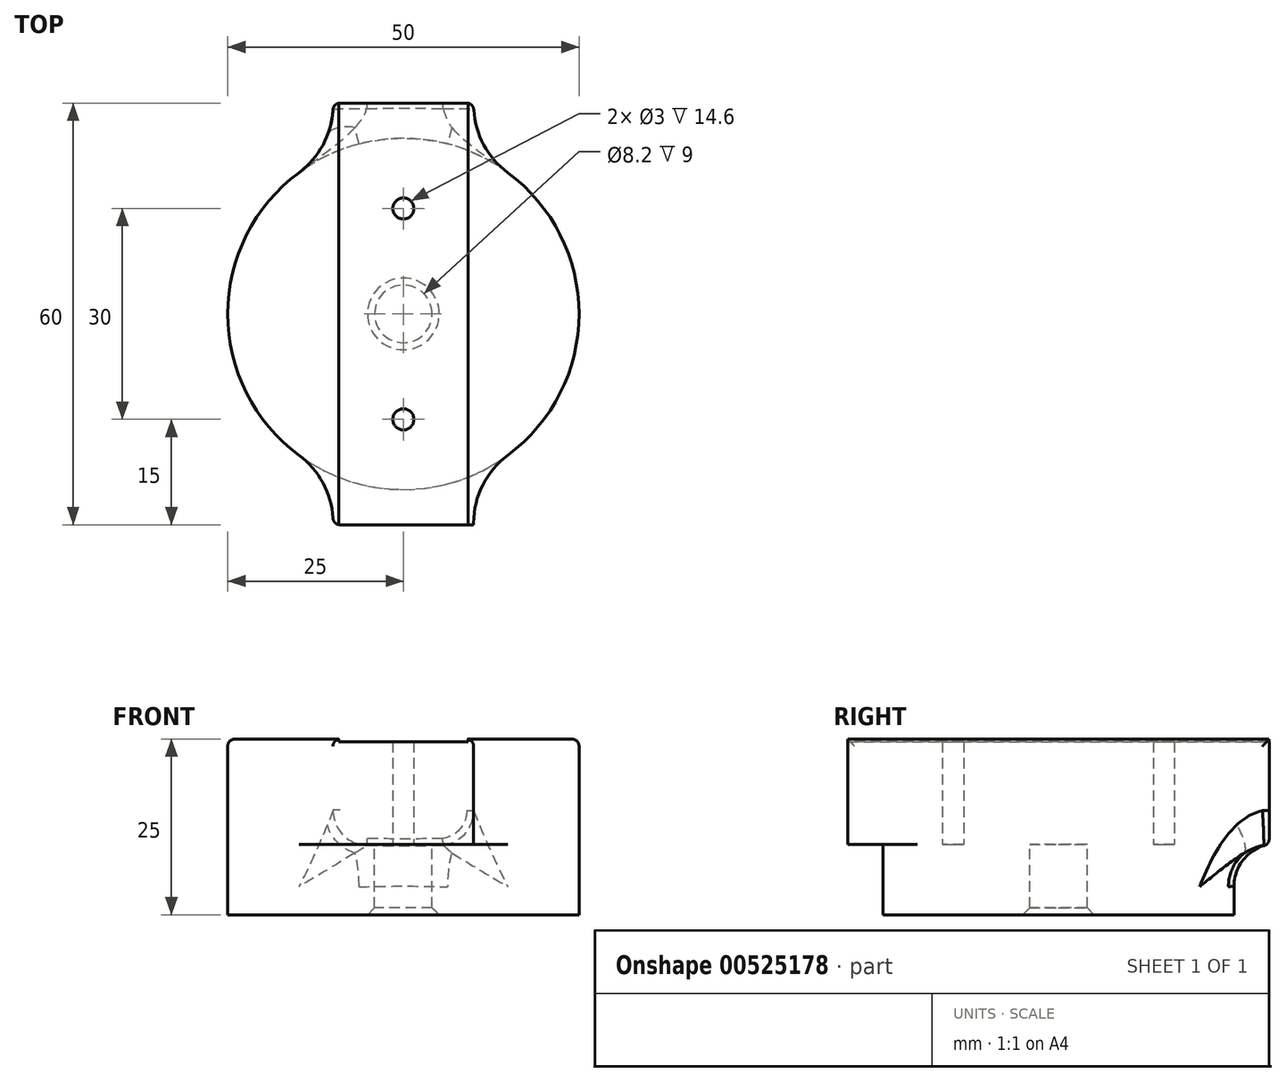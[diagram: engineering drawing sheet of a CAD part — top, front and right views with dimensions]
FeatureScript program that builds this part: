
annotation { "Feature Type Name" : "Feature", "Feature Type Description" : "" }
export const myFeature = defineFeature(function(context is Context, id is Id, definition is map)
    precondition{}
    {
        {
            var Q0;
            Q0=qCreatedBy(makeId("Top.planeOp"),FACE);
            var sketch = newSketch(context, id + "F0", { "sketchPlane" : qUnion([Q0])});
            skLineSegment(sketch, "E0.bottom", {"start": v(-10, 0) * mm, "end": v(10, 0) * mm});
            skLineSegment(sketch, "E0.top", {"start": v(-10, 30) * mm, "end": v(10, 30) * mm});
            skLineSegment(sketch, "E0.left", {"start": v(-10, 0) * mm, "end": v(-10, 30) * mm});
            skLineSegment(sketch, "E0.right", {"start": v(10, 0) * mm, "end": v(10, 30) * mm});
            skCircle(sketch, "E1", {"center": v(0, 15) * mm, "radius": 1.5 * mm});
            skCircle(sketch, "E2", {"center": v(0, 0) * mm, "radius": 25 * mm});
            skCircle(sketch, "E3", {"center": v(0, 0) * mm, "radius": 4.1 * mm});
            skLineSegment(sketch, "E4.1.0", {"start": v(10, -30) * mm, "end": v(-10, -30) * mm});
            skLineSegment(sketch, "E4.1.1", {"start": v(10, 0) * mm, "end": v(10, -30) * mm});
            skLineSegment(sketch, "E4.1.2", {"start": v(-10, 0) * mm, "end": v(-10, -30) * mm});
            skCircle(sketch, "E4.1.3", {"center": v(0, -15) * mm, "radius": 1.5 * mm});
            skSolve(sketch);
        }
        {
            var Q0;
            {var subQ1=sQuery(id+"F0.wireOp",EDGE,"E0.right");var subQ3=sQuery(id+"F0.wireOp",EDGE,"E2");var subQ4=makeQuery(id+"F0.imprint","INTERSECT",VERTEX,{"derivedFrom":[subQ1,subQ3]});Q0=makeQuery(id+"F0.imprint","IMPRINT",FACE,{"disambiguationData":[TD([[makeQuery(id+"F0.imprint","IMPRINT",EDGE,{"disambiguationData":[TD([[subQ4,1.0]])],"derivedFrom":subQ3}),1.0]])]});}
            var Q1;
            {var subQ1=sQuery(id+"F0.wireOp",EDGE,"E0.left");var subQ3=sQuery(id+"F0.wireOp",EDGE,"E2");var subQ4=makeQuery(id+"F0.imprint","INTERSECT",VERTEX,{"derivedFrom":[subQ1,subQ3]});Q1=makeQuery(id+"F0.imprint","IMPRINT",FACE,{"disambiguationData":[TD([[makeQuery(id+"F0.imprint","IMPRINT",EDGE,{"disambiguationData":[TD([[subQ4,-1.0]])],"derivedFrom":subQ3}),1.0]])]});}
            var Q2;
            Q2=makeQuery(id+"F0.imprint","IMPRINT",FACE,{"disambiguationData":[TD([[makeQuery(id+"F0.imprint","IMPRINT",EDGE,{"derivedFrom":sQuery(id+"F0.wireOp",EDGE,"E1")}),-1.0]])]});
            var Q3;
            {var subQ5=sQuery(id+"F0.wireOp",EDGE,"E4.1.0");Q3=makeQuery(id+"F0.imprint","IMPRINT",FACE,{"disambiguationData":[TD([[makeQuery(id+"F0.imprint","IMPRINT",EDGE,{"derivedFrom":subQ5}),-1.0]])]});}
            var Q4;
            Q4=makeQuery(id+"F0.imprint","IMPRINT",FACE,{"disambiguationData":[TD([[makeQuery(id+"F0.imprint","IMPRINT",EDGE,{"derivedFrom":sQuery(id+"F0.wireOp",EDGE,"E4.1.3")}),-1.0]])]});
            var Q5;
            {var subQ0=sQuery(id+"F0.wireOp",EDGE,"E3");var subQ1=sQuery(id+"F0.wireOp",EDGE,"E0.bottom");var subQ2=makeQuery(id+"F0.imprint","INTERSECT",VERTEX,{"disambiguationData":[OD(0.0)],"derivedFrom":[subQ1,subQ0]});Q5=makeQuery(id+"F0.imprint","IMPRINT",FACE,{"disambiguationData":[TD([[makeQuery(id+"F0.imprint","IMPRINT",EDGE,{"disambiguationData":[TD([[subQ2,-1.0]])],"derivedFrom":subQ1}),1.0]])]});}
            var Q6;
            {var subQ0=sQuery(id+"F0.wireOp",EDGE,"E3");var subQ1=sQuery(id+"F0.wireOp",EDGE,"E0.bottom");var subQ2=makeQuery(id+"F0.imprint","INTERSECT",VERTEX,{"disambiguationData":[OD(0.0)],"derivedFrom":[subQ1,subQ0]});Q6=makeQuery(id+"F0.imprint","IMPRINT",FACE,{"disambiguationData":[TD([[makeQuery(id+"F0.imprint","IMPRINT",EDGE,{"disambiguationData":[TD([[subQ2,-1.0]])],"derivedFrom":subQ1}),-1.0]])]});}
            var Q7;
            {var subQ0=sQuery(id+"F0.wireOp",EDGE,"E0.top");Q7=makeQuery(id+"F0.imprint","IMPRINT",FACE,{"disambiguationData":[TD([[makeQuery(id+"F0.imprint","IMPRINT",EDGE,{"derivedFrom":subQ0}),-1.0]])]});}
            extrude(context, id + "F1", {"entities" : qUnion([Q0, Q1, Q2, Q3, Q4, Q5, Q6, Q7]), "depth" : 14.6 * mm, "offsetDistance" : 25 * mm});
        }
        {
            var Q0;
            {var subQ1=sQuery(id+"F0.wireOp",EDGE,"E0.right");var subQ3=sQuery(id+"F0.wireOp",EDGE,"E2");var subQ4=makeQuery(id+"F0.imprint","INTERSECT",VERTEX,{"derivedFrom":[subQ1,subQ3]});Q0=makeQuery(id+"F0.imprint","IMPRINT",FACE,{"disambiguationData":[TD([[makeQuery(id+"F0.imprint","IMPRINT",EDGE,{"disambiguationData":[TD([[subQ4,1.0]])],"derivedFrom":subQ3}),1.0]])]});}
            var Q1;
            Q1=makeQuery(id+"F0.imprint","IMPRINT",FACE,{"disambiguationData":[TD([[makeQuery(id+"F0.imprint","IMPRINT",EDGE,{"derivedFrom":sQuery(id+"F0.wireOp",EDGE,"E4.1.3")}),-1.0]])]});
            var Q2;
            {var subQ1=sQuery(id+"F0.wireOp",EDGE,"E0.left");var subQ3=sQuery(id+"F0.wireOp",EDGE,"E2");var subQ4=makeQuery(id+"F0.imprint","INTERSECT",VERTEX,{"derivedFrom":[subQ1,subQ3]});Q2=makeQuery(id+"F0.imprint","IMPRINT",FACE,{"disambiguationData":[TD([[makeQuery(id+"F0.imprint","IMPRINT",EDGE,{"disambiguationData":[TD([[subQ4,-1.0]])],"derivedFrom":subQ3}),1.0]])]});}
            var Q3;
            Q3=makeQuery(id+"F0.imprint","IMPRINT",FACE,{"disambiguationData":[TD([[makeQuery(id+"F0.imprint","IMPRINT",EDGE,{"derivedFrom":sQuery(id+"F0.wireOp",EDGE,"E4.1.3")}),1.0]])]});
            var Q4;
            Q4=makeQuery(id+"F0.imprint","IMPRINT",FACE,{"disambiguationData":[TD([[makeQuery(id+"F0.imprint","IMPRINT",EDGE,{"derivedFrom":sQuery(id+"F0.wireOp",EDGE,"E1")}),-1.0]])]});
            var Q5;
            Q5=makeQuery(id+"F0.imprint","IMPRINT",FACE,{"disambiguationData":[TD([[makeQuery(id+"F0.imprint","IMPRINT",EDGE,{"derivedFrom":sQuery(id+"F0.wireOp",EDGE,"E1")}),1.0]])]});
            extrude(context, id + "F2", {"entities" : qUnion([Q0, Q1, Q2, Q3, Q4, Q5]), "operationType" : NewBodyOperationType.ADD, "oppositeDirection" : true, "depth" : 10 * mm, "offsetDistance" : 25 * mm});
        }
        {
            var Q0;
            Q0=makeQuery(id+"F1.opExtrude","CAP_FACE",FACE,{"disambiguationData":[OSD([sQuery(id+"F0.wireOp",EDGE,"E0.top"),sQuery(id+"F0.wireOp",EDGE,"E0.left"),sQuery(id+"F0.wireOp",EDGE,"E0.right"),sQuery(id+"F0.wireOp",EDGE,"E1"),sQuery(id+"F0.wireOp",EDGE,"E2"),sQuery(id+"F0.wireOp",EDGE,"E4.1.0"),sQuery(id+"F0.wireOp",EDGE,"E4.1.1"),sQuery(id+"F0.wireOp",EDGE,"E4.1.2"),sQuery(id+"F0.wireOp",EDGE,"E4.1.3")])],"isStart":false});
            var sketch = newSketch(context, id + "F3", { "sketchPlane" : qUnion([Q0])});
            skLineSegment(sketch, "E5.0", {"start": v(-9.2, 0) * mm, "end": v(-9.2, 30) * mm});
            skLineSegment(sketch, "E6.0", {"start": v(9.2, 0) * mm, "end": v(9.2, 30) * mm});
            skLineSegment(sketch, "E7.0", {"start": v(-9.2, 0) * mm, "end": v(-9.2, -30) * mm});
            skLineSegment(sketch, "E8.0", {"start": v(9.2, 0) * mm, "end": v(9.2, -30) * mm});
            skSolve(sketch);
        }
        {
            var Q0;
            {var subQ5=sQuery(id+"F3.wireOp",EDGE,"E5.0");Q0=makeQuery(id+"F3.imprint","IMPRINT",FACE,{"disambiguationData":[TD([[makeQuery(id+"F3.imprint","IMPRINT",EDGE,{"derivedFrom":subQ5}),1.0]])]});}
            var Q1;
            {var subQ5=sQuery(id+"F3.wireOp",EDGE,"E6.0");Q1=makeQuery(id+"F3.imprint","IMPRINT",FACE,{"disambiguationData":[TD([[makeQuery(id+"F3.imprint","IMPRINT",EDGE,{"derivedFrom":subQ5}),-1.0]])]});}
            extrude(context, id + "F4", {"entities" : qUnion([Q0, Q1]), "operationType" : NewBodyOperationType.ADD, "depth" : .4 * mm, "offsetDistance" : 25 * mm});
        }
        {
            var Q0;
            {var subQ0=sQuery(id+"F0.wireOp",EDGE,"E4.1.1");var subQ1=sQuery(id+"F0.wireOp",EDGE,"E2");Q0=makeQuery(id+"F4.boolean.opBoolean","MERGE",EDGE,{"derivedFrom":[makeQuery(id+"F1.opExtrude","SWEPT_EDGE",EDGE,{"disambiguationData":[OSD([subQ1,subQ0])]}),makeQuery(id+"F4.opExtrude","SWEPT_EDGE",EDGE,{"disambiguationData":[OSD([subQ1,subQ0])]})]});}
            var Q1;
            {var subQ0=sQuery(id+"F0.wireOp",EDGE,"E2");var subQ1=sQuery(id+"F0.wireOp",EDGE,"E0.right");Q1=makeQuery(id+"F4.boolean.opBoolean","MERGE",EDGE,{"derivedFrom":[makeQuery(id+"F1.opExtrude","SWEPT_EDGE",EDGE,{"disambiguationData":[OSD([subQ1,subQ0])]}),makeQuery(id+"F4.opExtrude","SWEPT_EDGE",EDGE,{"disambiguationData":[OSD([subQ1,subQ0])]})]});}
            var Q2;
            {var subQ0=sQuery(id+"F0.wireOp",EDGE,"E2");var subQ1=sQuery(id+"F0.wireOp",EDGE,"E0.left");Q2=makeQuery(id+"F4.boolean.opBoolean","MERGE",EDGE,{"derivedFrom":[makeQuery(id+"F1.opExtrude","SWEPT_EDGE",EDGE,{"disambiguationData":[OSD([subQ1,subQ0])]}),makeQuery(id+"F4.opExtrude","SWEPT_EDGE",EDGE,{"disambiguationData":[OSD([subQ1,subQ0])]})]});}
            var Q3;
            {var subQ0=sQuery(id+"F0.wireOp",EDGE,"E4.1.2");var subQ1=sQuery(id+"F0.wireOp",EDGE,"E2");Q3=makeQuery(id+"F4.boolean.opBoolean","MERGE",EDGE,{"derivedFrom":[makeQuery(id+"F1.opExtrude","SWEPT_EDGE",EDGE,{"disambiguationData":[OSD([subQ1,subQ0])]}),makeQuery(id+"F4.opExtrude","SWEPT_EDGE",EDGE,{"disambiguationData":[OSD([subQ1,subQ0])]})]});}
            fillet(context, id + "F5", {"entities" : qUnion([Q0, Q1, Q2, Q3]), "radius" : 12 * mm, "tangentPropagation" : true, "allowEdgeOverflow" : false});
        }
        {
            var Q0;
            {var subQ0=sQuery(id+"F0.wireOp",EDGE,"E4.1.1");var subQ1=sQuery(id+"F0.wireOp",EDGE,"E2");Q0=makeQuery(id+"F2.boolean.opBoolean","SPLIT",EDGE,{"disambiguationData":[TD([makeQuery(id+"F1.opExtrude","SWEPT_FACE",FACE,{"disambiguationData":[OSD([subQ0])]})])],"derivedFrom":makeQuery(id+"F2.opExtrude","CAP_EDGE",EDGE,{"disambiguationData":[OSD([subQ1])],"isStart":true})});}
            var Q1;
            {var subQ1=sQuery(id+"F0.wireOp",EDGE,"E2");var subQ2=sQuery(id+"F0.wireOp",EDGE,"E0.left");Q1=makeQuery(id+"F2.boolean.opBoolean","SPLIT",EDGE,{"disambiguationData":[TD([makeQuery(id+"F1.opExtrude","SWEPT_FACE",FACE,{"disambiguationData":[OSD([subQ2])]})])],"derivedFrom":makeQuery(id+"F2.opExtrude","CAP_EDGE",EDGE,{"disambiguationData":[OSD([subQ1])],"isStart":true})});}
            fillet(context, id + "F6", {"entities" : qUnion([Q0, Q1]), "radius" : 6 * mm, "tangentPropagation" : true, "allowEdgeOverflow" : false});
        }
        {
            var Q0;
            {var subQ0=sQuery(id+"F0.wireOp",EDGE,"E4.1.1");var subQ1=sQuery(id+"F0.wireOp",EDGE,"E2");Q0=makeQuery(id+"F6.opFillet","BLEND_EDGE",EDGE,{"blendedFrom":[makeQuery(id+"F2.boolean.opBoolean","SPLIT",EDGE,{"disambiguationData":[TD([makeQuery(id+"F1.opExtrude","SWEPT_FACE",FACE,{"disambiguationData":[OSD([subQ0])]})])],"derivedFrom":makeQuery(id+"F2.opExtrude","CAP_EDGE",EDGE,{"disambiguationData":[OSD([subQ1])],"isStart":true})}),makeQuery(id+"F5.opFillet","BLEND_FACE",FACE,{"disambiguationData":[OSD([subQ1,subQ0])]})],"blendedInto":[makeQuery(id+"F5.opFillet","BLEND_FACE",FACE,{"disambiguationData":[OSD([subQ1,subQ0])]})]});}
            var Q1;
            {var subQ0=sQuery(id+"F0.wireOp",EDGE,"E4.1.2");var subQ1=sQuery(id+"F0.wireOp",EDGE,"E2");var subQ2=sQuery(id+"F0.wireOp",EDGE,"E4.1.1");Q1=makeQuery(id+"F6.opFillet","BLEND_EDGE",EDGE,{"blendedFrom":[makeQuery(id+"F2.boolean.opBoolean","SPLIT",EDGE,{"disambiguationData":[TD([makeQuery(id+"F1.opExtrude","SWEPT_FACE",FACE,{"disambiguationData":[OSD([subQ2])]})])],"derivedFrom":makeQuery(id+"F2.opExtrude","CAP_EDGE",EDGE,{"disambiguationData":[OSD([subQ1])],"isStart":true})}),makeQuery(id+"F5.opFillet","BLEND_FACE",FACE,{"disambiguationData":[OSD([subQ1,subQ0])]})],"blendedInto":[makeQuery(id+"F5.opFillet","BLEND_FACE",FACE,{"disambiguationData":[OSD([subQ1,subQ0])]})]});}
            var Q2;
            {var subQ0=sQuery(id+"F0.wireOp",EDGE,"E2");var subQ1=sQuery(id+"F0.wireOp",EDGE,"E0.right");var subQ2=sQuery(id+"F0.wireOp",EDGE,"E0.left");Q2=makeQuery(id+"F6.opFillet","BLEND_EDGE",EDGE,{"blendedFrom":[makeQuery(id+"F2.boolean.opBoolean","SPLIT",EDGE,{"disambiguationData":[TD([makeQuery(id+"F1.opExtrude","SWEPT_FACE",FACE,{"disambiguationData":[OSD([subQ2])]})])],"derivedFrom":makeQuery(id+"F2.opExtrude","CAP_EDGE",EDGE,{"disambiguationData":[OSD([subQ0])],"isStart":true})}),makeQuery(id+"F5.opFillet","BLEND_FACE",FACE,{"disambiguationData":[OSD([subQ1,subQ0])]})],"blendedInto":[makeQuery(id+"F5.opFillet","BLEND_FACE",FACE,{"disambiguationData":[OSD([subQ1,subQ0])]})]});}
            var Q3;
            {var subQ0=sQuery(id+"F0.wireOp",EDGE,"E2");var subQ1=sQuery(id+"F0.wireOp",EDGE,"E0.left");Q3=makeQuery(id+"F6.opFillet","BLEND_EDGE",EDGE,{"blendedFrom":[makeQuery(id+"F2.boolean.opBoolean","SPLIT",EDGE,{"disambiguationData":[TD([makeQuery(id+"F1.opExtrude","SWEPT_FACE",FACE,{"disambiguationData":[OSD([subQ1])]})])],"derivedFrom":makeQuery(id+"F2.opExtrude","CAP_EDGE",EDGE,{"disambiguationData":[OSD([subQ0])],"isStart":true})}),makeQuery(id+"F5.opFillet","BLEND_FACE",FACE,{"disambiguationData":[OSD([subQ1,subQ0])]})],"blendedInto":[makeQuery(id+"F5.opFillet","BLEND_FACE",FACE,{"disambiguationData":[OSD([subQ1,subQ0])]})]});}
            fillet(context, id + "F7", {"entities" : qUnion([Q0, Q1, Q2, Q3]), "radius" : 5 * mm, "tangentPropagation" : true, "allowEdgeOverflow" : false});
        }
        {
            var Q0;
            {var subQ0=sQuery(id+"F0.wireOp",EDGE,"E2");Q0=makeQuery(id+"F4.opExtrude","CAP_EDGE",EDGE,{"disambiguationData":[OSD([subQ0]),TDD([makeQuery(id+"F3.imprint","IMPRINT",EDGE,{"derivedFrom":makeQuery(id+"F1.opExtrude","CAP_EDGE",EDGE,{"disambiguationData":[OSD([subQ0]),TDD([makeQuery(id+"F0.imprint","IMPRINT",EDGE,{"disambiguationData":[TD([[makeQuery(id+"F0.imprint","INTERSECT",VERTEX,{"derivedFrom":[sQuery(id+"F0.wireOp",EDGE,"E0.right"),subQ0]}),1.0]])],"derivedFrom":subQ0})])],"isStart":false})})])],"isStart":false});}
            var Q1;
            {var subQ0=sQuery(id+"F0.wireOp",EDGE,"E2");var subQ1=sQuery(id+"F0.wireOp",EDGE,"E0.left");Q1=makeQuery(id+"F5.opFillet","BLEND_EDGE",EDGE,{"blendedFrom":[makeQuery(id+"F4.boolean.opBoolean","MERGE",EDGE,{"derivedFrom":[makeQuery(id+"F1.opExtrude","SWEPT_EDGE",EDGE,{"disambiguationData":[OSD([subQ1,subQ0])]}),makeQuery(id+"F4.opExtrude","SWEPT_EDGE",EDGE,{"disambiguationData":[OSD([subQ1,subQ0])]})]}),makeQuery(id+"F4.opExtrude","CAP_FACE",FACE,{"disambiguationData":[OSD([sQuery(id+"F0.wireOp",EDGE,"E0.top"),subQ1,subQ0,sQuery(id+"F0.wireOp",EDGE,"E4.1.0"),sQuery(id+"F0.wireOp",EDGE,"E4.1.2"),sQuery(id+"F3.wireOp",EDGE,"E5.0"),sQuery(id+"F3.wireOp",EDGE,"E7.0")])],"isStart":false})],"blendedInto":[makeQuery(id+"F4.opExtrude","CAP_FACE",FACE,{"disambiguationData":[OSD([sQuery(id+"F0.wireOp",EDGE,"E0.top"),subQ1,subQ0,sQuery(id+"F0.wireOp",EDGE,"E4.1.0"),sQuery(id+"F0.wireOp",EDGE,"E4.1.2"),sQuery(id+"F3.wireOp",EDGE,"E5.0"),sQuery(id+"F3.wireOp",EDGE,"E7.0")])],"isStart":false})]});}
            fillet(context, id + "F8", {"entities" : qUnion([Q0, Q1]), "radius" : 1 * mm, "tangentPropagation" : true, "allowEdgeOverflow" : false});
        }
        {
            var Q0;
            {var subQ0=sQuery(id+"F0.wireOp",EDGE,"E4.1.2");var subQ1=sQuery(id+"F0.wireOp",EDGE,"E4.1.0");var subQ2=makeQuery(id+"F1.opExtrude","CAP_EDGE",EDGE,{"disambiguationData":[OSD([subQ1])],"isStart":false});var subQ3=sQuery(id+"F0.wireOp",EDGE,"E4.1.1");var subQ4=sQuery(id+"F0.wireOp",EDGE,"E2");Q0=makeQuery(id+"F6.opFillet","BLEND_EDGE",EDGE,{"blendedFrom":[makeQuery(id+"F2.boolean.opBoolean","SPLIT",EDGE,{"disambiguationData":[TD([makeQuery(id+"F1.opExtrude","SWEPT_FACE",FACE,{"disambiguationData":[OSD([subQ3])]})])],"derivedFrom":makeQuery(id+"F2.opExtrude","CAP_EDGE",EDGE,{"disambiguationData":[OSD([subQ4])],"isStart":true})}),makeQuery(id+"F4.boolean.opBoolean","MERGE",FACE,{"derivedFrom":[makeQuery(id+"F1.opExtrude","SWEPT_FACE",FACE,{"disambiguationData":[OSD([subQ1])]}),makeQuery(id+"F4.opExtrude","SWEPT_FACE",FACE,{"disambiguationData":[OSD([subQ1]),TDD([makeQuery(id+"F3.imprint","IMPRINT",EDGE,{"disambiguationData":[TD([[makeQuery(id+"F3.imprint","INTERSECT",VERTEX,{"derivedFrom":[subQ2,makeQuery(id+"F1.opExtrude","CAP_EDGE",EDGE,{"disambiguationData":[OSD([subQ3])],"isStart":false})]}),-1.0]])],"derivedFrom":subQ2})])]}),makeQuery(id+"F4.opExtrude","SWEPT_FACE",FACE,{"disambiguationData":[OSD([subQ1]),TDD([makeQuery(id+"F3.imprint","IMPRINT",EDGE,{"disambiguationData":[TD([[makeQuery(id+"F3.imprint","INTERSECT",VERTEX,{"derivedFrom":[subQ2,makeQuery(id+"F1.opExtrude","CAP_EDGE",EDGE,{"disambiguationData":[OSD([subQ0])],"isStart":false})]}),1.0]])],"derivedFrom":subQ2})])]})]})],"blendedInto":[makeQuery(id+"F4.boolean.opBoolean","MERGE",FACE,{"derivedFrom":[makeQuery(id+"F1.opExtrude","SWEPT_FACE",FACE,{"disambiguationData":[OSD([subQ1])]}),makeQuery(id+"F4.opExtrude","SWEPT_FACE",FACE,{"disambiguationData":[OSD([subQ1]),TDD([makeQuery(id+"F3.imprint","IMPRINT",EDGE,{"disambiguationData":[TD([[makeQuery(id+"F3.imprint","INTERSECT",VERTEX,{"derivedFrom":[subQ2,makeQuery(id+"F1.opExtrude","CAP_EDGE",EDGE,{"disambiguationData":[OSD([subQ3])],"isStart":false})]}),-1.0]])],"derivedFrom":subQ2})])]}),makeQuery(id+"F4.opExtrude","SWEPT_FACE",FACE,{"disambiguationData":[OSD([subQ1]),TDD([makeQuery(id+"F3.imprint","IMPRINT",EDGE,{"disambiguationData":[TD([[makeQuery(id+"F3.imprint","INTERSECT",VERTEX,{"derivedFrom":[subQ2,makeQuery(id+"F1.opExtrude","CAP_EDGE",EDGE,{"disambiguationData":[OSD([subQ0])],"isStart":false})]}),1.0]])],"derivedFrom":subQ2})])]})]})]});}
            var Q1;
            {var subQ0=sQuery(id+"F0.wireOp",EDGE,"E4.1.2");var subQ1=sQuery(id+"F0.wireOp",EDGE,"E4.1.0");Q1=makeQuery(id+"F4.boolean.opBoolean","MERGE",EDGE,{"derivedFrom":[makeQuery(id+"F1.opExtrude","SWEPT_EDGE",EDGE,{"disambiguationData":[OSD([subQ1,subQ0])]}),makeQuery(id+"F4.opExtrude","SWEPT_EDGE",EDGE,{"disambiguationData":[OSD([subQ1,subQ0])]})]});}
            var Q2;
            {var subQ0=sQuery(id+"F0.wireOp",EDGE,"E0.right");var subQ1=sQuery(id+"F0.wireOp",EDGE,"E0.top");Q2=makeQuery(id+"F4.boolean.opBoolean","MERGE",EDGE,{"derivedFrom":[makeQuery(id+"F1.opExtrude","SWEPT_EDGE",EDGE,{"disambiguationData":[OSD([subQ1,subQ0])]}),makeQuery(id+"F4.opExtrude","SWEPT_EDGE",EDGE,{"disambiguationData":[OSD([subQ1,subQ0])]})]});}
            var Q3;
            {var subQ0=sQuery(id+"F0.wireOp",EDGE,"E0.right");var subQ1=sQuery(id+"F0.wireOp",EDGE,"E0.top");var subQ2=makeQuery(id+"F1.opExtrude","CAP_EDGE",EDGE,{"disambiguationData":[OSD([subQ1])],"isStart":false});var subQ3=sQuery(id+"F0.wireOp",EDGE,"E0.left");var subQ4=sQuery(id+"F0.wireOp",EDGE,"E2");Q3=makeQuery(id+"F6.opFillet","BLEND_EDGE",EDGE,{"blendedFrom":[makeQuery(id+"F2.boolean.opBoolean","SPLIT",EDGE,{"disambiguationData":[TD([makeQuery(id+"F1.opExtrude","SWEPT_FACE",FACE,{"disambiguationData":[OSD([subQ3])]})])],"derivedFrom":makeQuery(id+"F2.opExtrude","CAP_EDGE",EDGE,{"disambiguationData":[OSD([subQ4])],"isStart":true})}),makeQuery(id+"F4.boolean.opBoolean","MERGE",FACE,{"derivedFrom":[makeQuery(id+"F1.opExtrude","SWEPT_FACE",FACE,{"disambiguationData":[OSD([subQ1])]}),makeQuery(id+"F4.opExtrude","SWEPT_FACE",FACE,{"disambiguationData":[OSD([subQ1]),TDD([makeQuery(id+"F3.imprint","IMPRINT",EDGE,{"disambiguationData":[TD([[makeQuery(id+"F3.imprint","INTERSECT",VERTEX,{"derivedFrom":[subQ2,makeQuery(id+"F1.opExtrude","CAP_EDGE",EDGE,{"disambiguationData":[OSD([subQ3])],"isStart":false})]}),-1.0]])],"derivedFrom":subQ2})])]}),makeQuery(id+"F4.opExtrude","SWEPT_FACE",FACE,{"disambiguationData":[OSD([subQ1]),TDD([makeQuery(id+"F3.imprint","IMPRINT",EDGE,{"disambiguationData":[TD([[makeQuery(id+"F3.imprint","INTERSECT",VERTEX,{"derivedFrom":[subQ2,makeQuery(id+"F1.opExtrude","CAP_EDGE",EDGE,{"disambiguationData":[OSD([subQ0])],"isStart":false})]}),1.0]])],"derivedFrom":subQ2})])]})]})],"blendedInto":[makeQuery(id+"F4.boolean.opBoolean","MERGE",FACE,{"derivedFrom":[makeQuery(id+"F1.opExtrude","SWEPT_FACE",FACE,{"disambiguationData":[OSD([subQ1])]}),makeQuery(id+"F4.opExtrude","SWEPT_FACE",FACE,{"disambiguationData":[OSD([subQ1]),TDD([makeQuery(id+"F3.imprint","IMPRINT",EDGE,{"disambiguationData":[TD([[makeQuery(id+"F3.imprint","INTERSECT",VERTEX,{"derivedFrom":[subQ2,makeQuery(id+"F1.opExtrude","CAP_EDGE",EDGE,{"disambiguationData":[OSD([subQ3])],"isStart":false})]}),-1.0]])],"derivedFrom":subQ2})])]}),makeQuery(id+"F4.opExtrude","SWEPT_FACE",FACE,{"disambiguationData":[OSD([subQ1]),TDD([makeQuery(id+"F3.imprint","IMPRINT",EDGE,{"disambiguationData":[TD([[makeQuery(id+"F3.imprint","INTERSECT",VERTEX,{"derivedFrom":[subQ2,makeQuery(id+"F1.opExtrude","CAP_EDGE",EDGE,{"disambiguationData":[OSD([subQ0])],"isStart":false})]}),1.0]])],"derivedFrom":subQ2})])]})]})]});}
            fillet(context, id + "F9", {"entities" : qUnion([Q0, Q1, Q2, Q3]), "radius" : 1 * mm, "tangentPropagation" : true, "allowEdgeOverflow" : false});
        }
        {
            var Q0;
            Q0=makeQuery(id+"F2.opExtrude","CAP_EDGE",EDGE,{"disambiguationData":[OSD([sQuery(id+"F0.wireOp",EDGE,"E3")])],"isStart":false});
            chamfer(context, id + "F10", {"entities" : qUnion([Q0]), "width" : 1 * mm, "tangentPropagation" : true});
        }
    });
